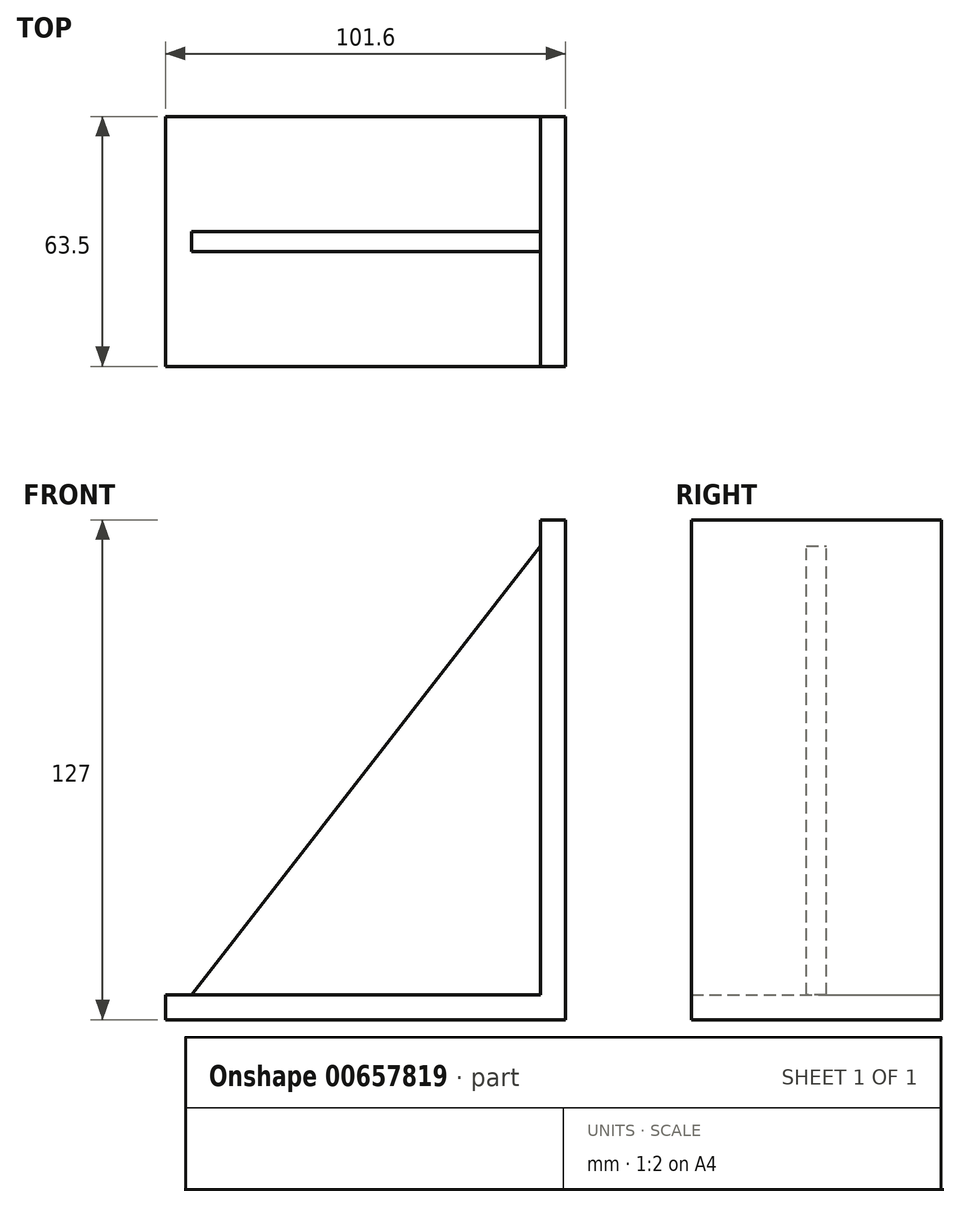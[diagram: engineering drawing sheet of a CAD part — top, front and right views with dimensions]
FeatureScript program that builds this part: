
annotation { "Feature Type Name" : "Feature", "Feature Type Description" : "" }
export const myFeature = defineFeature(function(context is Context, id is Id, definition is map)
    precondition{}
    {
        {
            var Q0;
            Q0=qCreatedBy(makeId("Front.planeOp"),FACE);
            var sketch = newSketch(context, id + "F0", { "sketchPlane" : qUnion([Q0])});
            skLineSegment(sketch, "E0", {"start": v(-95.25, 0) * mm, "end": v(6.35, 0) * mm});
            skLineSegment(sketch, "E1", {"start": v(6.35, 0) * mm, "end": v(6.35, 127) * mm});
            skLineSegment(sketch, "E2", {"start": v(6.35, 127) * mm, "end": v(0, 127) * mm});
            skLineSegment(sketch, "E3", {"start": v(0, 127) * mm, "end": v(0, 6.35) * mm});
            skLineSegment(sketch, "E4", {"start": v(0, 6.35) * mm, "end": v(-95.25, 6.35) * mm});
            skLineSegment(sketch, "E5", {"start": v(-95.25, 6.35) * mm, "end": v(-95.25, 0) * mm});
            skSolve(sketch);
        }
        {
            var Q0;
            Q0=makeQuery(id+"F0.imprint","IMPRINT",FACE,{"disambiguationData":[TD([[makeQuery(id+"F0.imprint","IMPRINT",EDGE,{"derivedFrom":sQuery(id+"F0.wireOp",EDGE,"E0")}),1.0]])]});
            extrude(context, id + "F1", {"entities" : qUnion([Q0]), "endBound" : BoundingType.SYMMETRIC, "depth" : 63.5 * mm, "offsetDistance" : 25.4 * mm});
        }
        {
            var Q0;
            Q0=qCreatedBy(makeId("Front.planeOp"),FACE);
            var sketch = newSketch(context, id + "F2", { "sketchPlane" : qUnion([Q0])});
            skLineSegment(sketch, "E6", {"start": v(0, 120.39) * mm, "end": v(-88.9, 6.09) * mm});
            skLineSegment(sketch, "E7", {"start": v(-88.9, 6.09) * mm, "end": v(0, 6.09) * mm});
            skLineSegment(sketch, "E8", {"start": v(0, 6.09) * mm, "end": v(0, 120.39) * mm});
            skSolve(sketch);
        }
        {
            var Q0;
            Q0=makeQuery(id+"F2.imprint","IMPRINT",FACE,{"disambiguationData":[TD([[makeQuery(id+"F2.imprint","IMPRINT",EDGE,{"derivedFrom":sQuery(id+"F2.wireOp",EDGE,"E6")}),1.0]])]});
            extrude(context, id + "F3", {"entities" : qUnion([Q0]), "operationType" : NewBodyOperationType.ADD, "endBound" : BoundingType.SYMMETRIC, "depth" : 5.08 * mm, "offsetDistance" : 25.4 * mm});
        }
    });
